# Revit family: 205_SQLL-25-_-600
name_source: partatom
category: Duct Accessories
units: mm (PartAtom-declared; Revit-internal decimal feet)

## family parameters
Always vertical = Yes
Cut with Voids When Loaded = No
Part Type = Breaks Into
Round Connector Dimension = Use Diameter
Shared = No
Work Plane-Based = No

## types (10) — shared parameters
CAT0 = Yes
Description = ROUND SILENCER IN THE RECTANGULAR CASING
L2D = 600 mm  [stored 1.9685 ft]
LL = 300 mm  [stored 0.984252 ft]
Manufacturer = Alnor
QmdConnectorList = 201;D;202;D
URL = http://www.ventilation-alnor.co.uk
magiPartTypeId = 205
magiProductFamilyId = SQLL-25-*-600

## per-type parameters (varying)
| type | CBB | CH | CHH | D | H2D | W2D |
| SQLL-25-100-600 | 75 mm  [stored 0.246063 ft] | 150 mm  [stored 0.492126 ft] | 75 mm  [stored 0.246063 ft] | 100 mm | 150 mm  [stored 0.492126 ft] | 150 mm  [stored 0.492126 ft] |
| SQLL-25-630-600 | 340 mm | 680 mm | 340 mm | 630 mm | 680 mm | 680 mm |
| SQLL-25-500-600 | 275 mm | 550 mm | 275 mm | 500 mm | 550 mm | 550 mm |
| SQLL-25-450-600 | 250 mm | 500 mm | 250 mm | 450 mm | 500 mm | 500 mm |
| SQLL-25-400-600 | 225 mm | 450 mm | 225 mm | 400 mm | 450 mm | 450 mm |
| SQLL-25-315-600 | 183 mm | 365 mm | 183 mm | 315 mm | 365 mm | 365 mm |
| SQLL-25-250-600 | 150 mm  [stored 0.492126 ft] | 300 mm  [stored 0.984252 ft] | 150 mm  [stored 0.492126 ft] | 250 mm | 300 mm  [stored 0.984252 ft] | 300 mm  [stored 0.984252 ft] |
| SQLL-25-200-600 | 125 mm | 250 mm | 125 mm | 200 mm | 250 mm | 250 mm |
| SQLL-25-160-600 | 105 mm | 210 mm | 105 mm | 160 mm | 210 mm | 210 mm |
| SQLL-25-125-600 | 88 mm | 175 mm | 88 mm | 120 mm | 175 mm | 175 mm |

note: column(s) folded — value = type name in every type: MC Product Code, magiProductId

note: [stored X ft] marks values corroborated as IEEE doubles in the binary element streams (Revit-internal decimal feet)

## geometry (parser evidence)
native form markers: Blend x4, Sweep x2
no freeform markers — native parametric forms only
